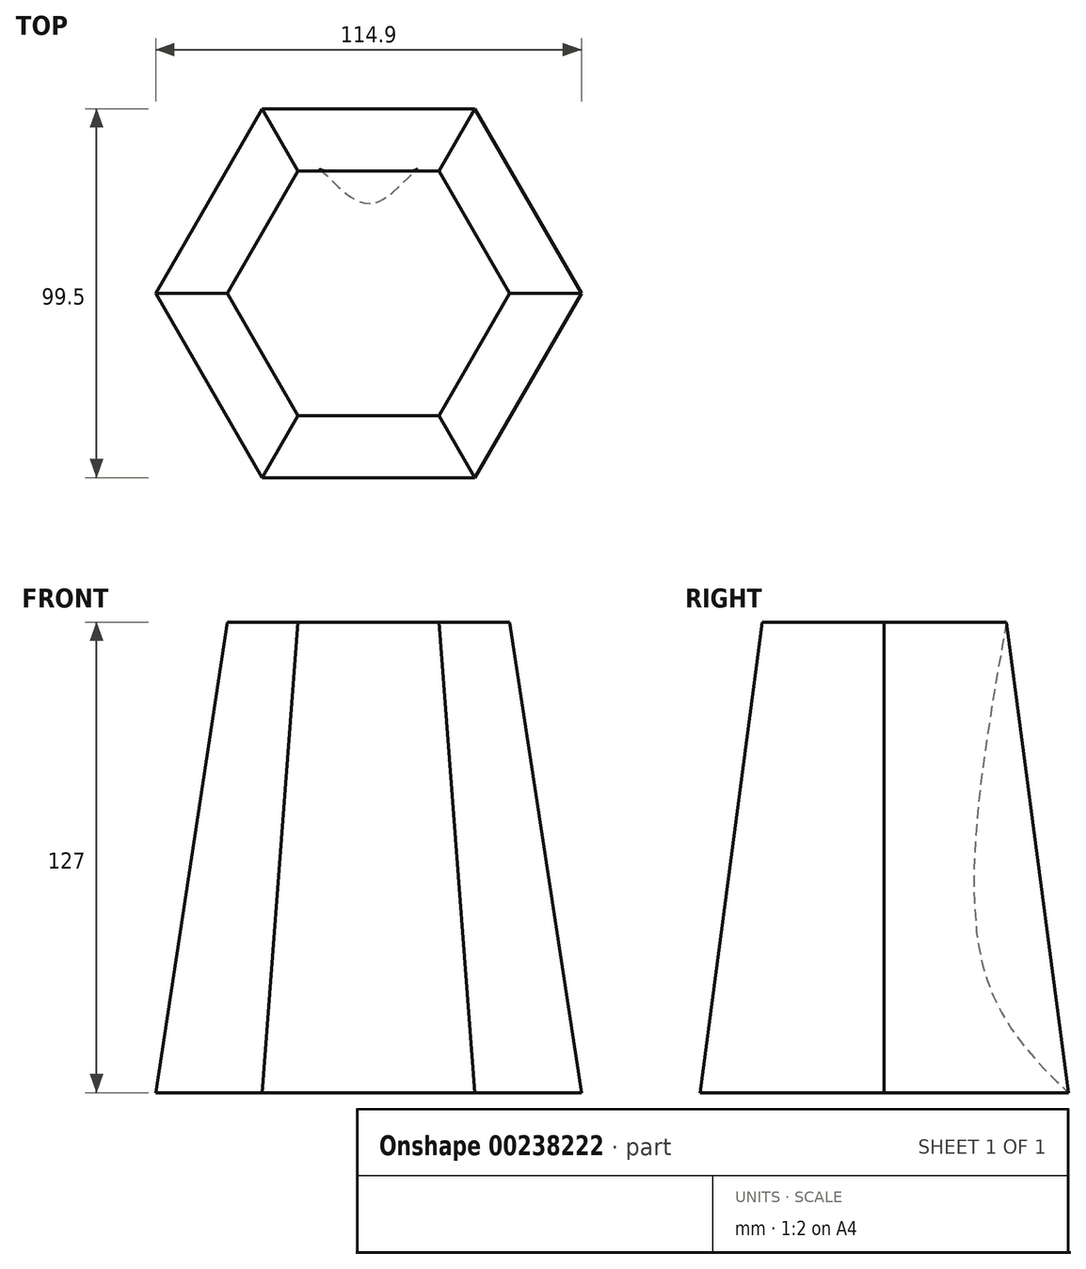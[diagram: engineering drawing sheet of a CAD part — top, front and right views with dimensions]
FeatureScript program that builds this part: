
annotation { "Feature Type Name" : "Feature", "Feature Type Description" : "" }
export const myFeature = defineFeature(function(context is Context, id is Id, definition is map)
    precondition{}
    {
        {
            var Q0;
            Q0=qCreatedBy(makeId("Top.planeOp"),FACE);
            cPlane(context, id + "F0", {"entities" : qUnion([Q0]), "cplaneType" : CPlaneType.OFFSET, "offset" : 127 * mm, "width" : 152.4 * mm, "height" : 152.4 * mm});
        }
        {
            var Q0;
            Q0=qCreatedBy(makeId("Top.planeOp"),FACE);
            var sketch = newSketch(context, id + "F1", { "sketchPlane" : qUnion([Q0])});
            skCircle(sketch, "E0.cCircle", {"center": v(0, 0) * mm, "radius": 49.75 * mm, "construction": true});
            skLineSegment(sketch, "E0.0", {"start": v(-28.73, 49.75) * mm, "end": v(28.73, 49.75) * mm});
            skLineSegment(sketch, "E0.1", {"start": v(28.73, 49.75) * mm, "end": v(57.45, 0) * mm});
            skLineSegment(sketch, "E0.2", {"start": v(57.45, 0) * mm, "end": v(28.73, -49.75) * mm});
            skLineSegment(sketch, "E0.3", {"start": v(28.73, -49.75) * mm, "end": v(-28.73, -49.75) * mm});
            skLineSegment(sketch, "E0.4", {"start": v(-28.73, -49.75) * mm, "end": v(-57.45, 0) * mm});
            skLineSegment(sketch, "E0.5", {"start": v(-57.45, 0) * mm, "end": v(-28.73, 49.75) * mm});
            skPoint(sketch, "E0.0.midPoint", {"position": v(0, 49.75) * mm});
            skSolve(sketch);
        }
        {
            var Q0;
            Q0=qCreatedBy(id+"F0.planeOp",FACE);
            var sketch = newSketch(context, id + "F2", { "sketchPlane" : qUnion([Q0])});
            skCircle(sketch, "E1.cCircle", {"center": v(0, 0) * mm, "radius": 33 * mm, "construction": true});
            skLineSegment(sketch, "E1.0", {"start": v(-19.05, 33) * mm, "end": v(19.05, 33) * mm});
            skLineSegment(sketch, "E1.1", {"start": v(19.05, 33) * mm, "end": v(38.1, 0) * mm});
            skLineSegment(sketch, "E1.2", {"start": v(38.1, 0) * mm, "end": v(19.05, -33) * mm});
            skLineSegment(sketch, "E1.3", {"start": v(19.05, -33) * mm, "end": v(-19.05, -33) * mm});
            skLineSegment(sketch, "E1.4", {"start": v(-19.05, -33) * mm, "end": v(-38.1, 0) * mm});
            skLineSegment(sketch, "E1.5", {"start": v(-38.1, 0) * mm, "end": v(-19.05, 33) * mm});
            skPoint(sketch, "E1.0.midPoint", {"position": v(0, 33) * mm});
            skSolve(sketch);
        }
        {
            var Q0;
            Q0=qCreatedBy(makeId("Right.planeOp"),FACE);
            var sketch = newSketch(context, id + "F3", { "sketchPlane" : qUnion([Q0])});
            skFitSpline(sketch, "E2", {"points": [v(49.75, 0) * mm, v(26.6, 34.3) * mm, v(33, 127) * mm], "startDerivative": vector(-75.26, 71.17) * mm, "endDerivative": vector(31.4, 176.34) * mm});
            skSolve(sketch);
        }
        {
            var Q0;
            Q0=makeQuery(id+"F1.imprint","IMPRINT",FACE,{"disambiguationData":[TD([[makeQuery(id+"F1.imprint","IMPRINT",EDGE,{"derivedFrom":sQuery(id+"F1.wireOp",EDGE,"E0.0")}),-1.0]])]});
            var Q1;
            Q1=makeQuery(id+"F2.imprint","IMPRINT",FACE,{"disambiguationData":[TD([[makeQuery(id+"F2.imprint","IMPRINT",EDGE,{"derivedFrom":sQuery(id+"F2.wireOp",EDGE,"E1.0")}),-1.0]])]});
            var Q2;
            Q2 = qConstructionFilter(qBodyType(qCreatedBy(id + "F3" ,EDGE), BodyType.WIRE), ConstructionObject.NO);
            loft(context, id + "F4", {"curveCount" : 10, "trimEnds" : true, "addGuides" : true, "sheetProfilesArray" : [{ "sheetProfileEntities" : qUnion([Q0]) }, { "sheetProfileEntities" : qUnion([Q1]) }], "thickness1" : 6.35 * mm, "thickness2" : 0 * mm, "thickness" : 6.35 * mm, "guidesArray" : [{ "guideEntities" : qUnion([Q2]), "guideDerivativeType" : LoftGuideDerivativeType.DEFAULT, "guideDerivativeMagnitude" : 1 }], "trimGuidesByProfiles" : true});
        }
    });
